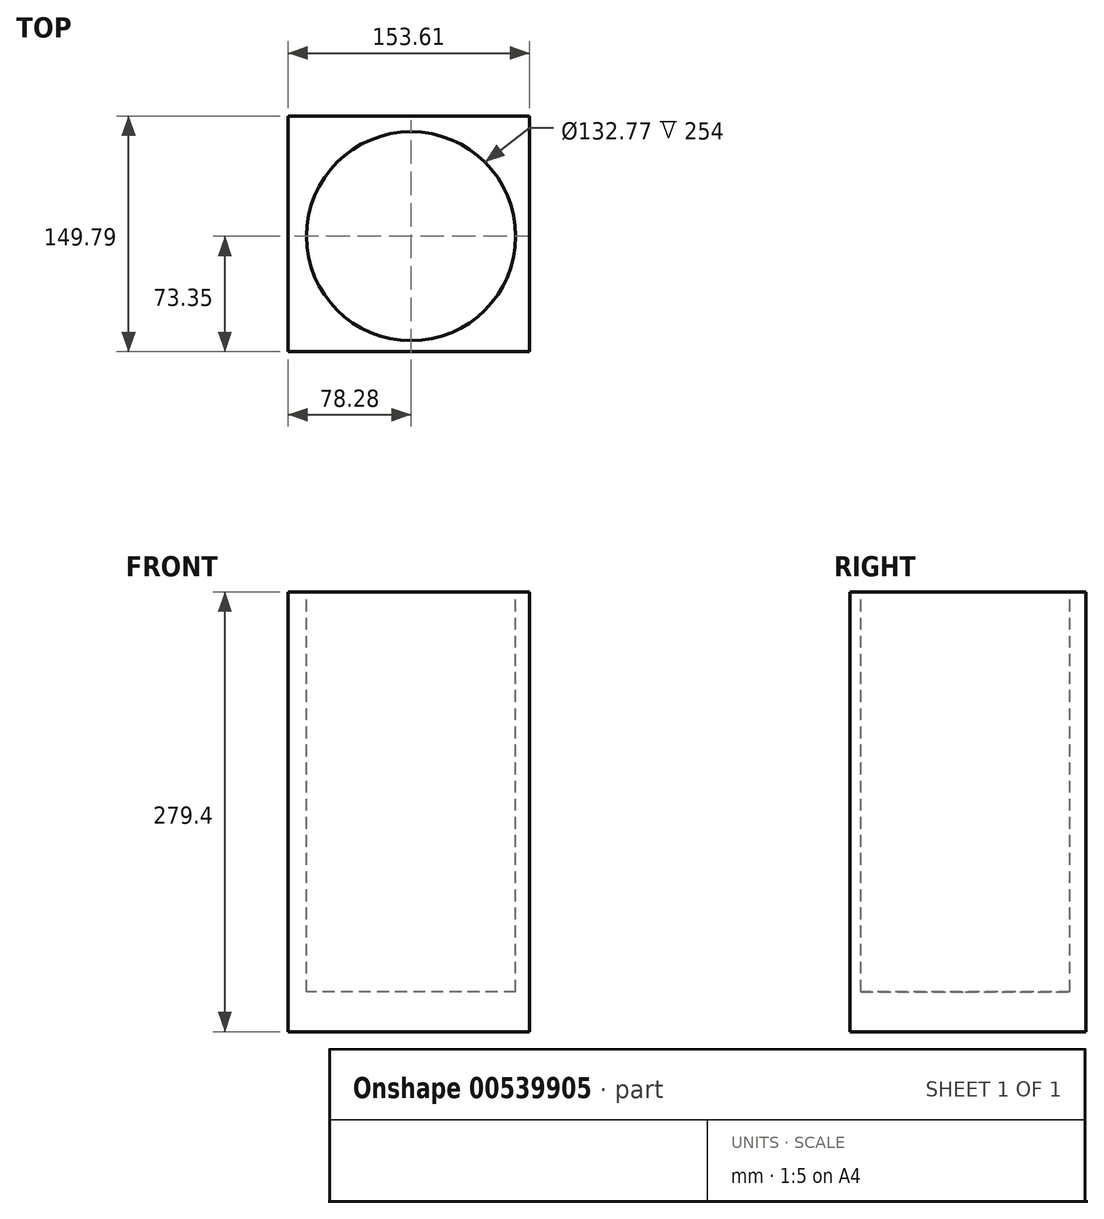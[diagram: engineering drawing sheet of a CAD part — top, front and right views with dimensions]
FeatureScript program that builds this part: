
annotation { "Feature Type Name" : "Feature", "Feature Type Description" : "" }
export const myFeature = defineFeature(function(context is Context, id is Id, definition is map)
    precondition{}
    {
        {
            var Q0;
            Q0=qCreatedBy(makeId("Top.planeOp"),FACE);
            var sketch = newSketch(context, id + "F0", { "sketchPlane" : qUnion([Q0])});
            skLineSegment(sketch, "E0.bottom", {"start": v(75.33, -73.35) * mm, "end": v(-78.28, -73.35) * mm});
            skLineSegment(sketch, "E0.top", {"start": v(75.33, 76.44) * mm, "end": v(-78.28, 76.44) * mm});
            skLineSegment(sketch, "E0.left", {"start": v(75.33, -73.35) * mm, "end": v(75.33, 76.44) * mm});
            skLineSegment(sketch, "E0.right", {"start": v(-78.28, -73.35) * mm, "end": v(-78.28, 76.44) * mm});
            skSolve(sketch);
        }
        {
            var Q0;
            Q0=makeQuery(id+"F0.imprint","IMPRINT",FACE,{"disambiguationData":[TD([[makeQuery(id+"F0.imprint","IMPRINT",EDGE,{"derivedFrom":sQuery(id+"F0.wireOp",EDGE,"E0.bottom")}),-1.0]])]});
            extrude(context, id + "F1", {"entities" : qUnion([Q0]), "depth" : 279.4 * mm, "offsetDistance" : 25.4 * mm});
        }
        {
            var Q0;
            Q0=makeQuery(id+"F1.opExtrude","CAP_FACE",FACE,{"disambiguationData":[OSD([sQuery(id+"F0.wireOp",EDGE,"E0.bottom"),sQuery(id+"F0.wireOp",EDGE,"E0.top"),sQuery(id+"F0.wireOp",EDGE,"E0.left"),sQuery(id+"F0.wireOp",EDGE,"E0.right")])],"isStart":false});
            var sketch = newSketch(context, id + "F2", { "sketchPlane" : qUnion([Q0])});
            skCircle(sketch, "E1", {"center": v(0, 0) * mm, "radius": 66.39 * mm});
            skSolve(sketch);
        }
        {
            var Q0;
            Q0=makeQuery(id+"F2.imprint","IMPRINT",FACE,{"disambiguationData":[TD([[makeQuery(id+"F2.imprint","IMPRINT",EDGE,{"derivedFrom":sQuery(id+"F2.wireOp",EDGE,"E1")}),1.0]])]});
            extrude(context, id + "F3", {"entities" : qUnion([Q0]), "operationType" : NewBodyOperationType.REMOVE, "oppositeDirection" : true, "depth" : 254 * mm, "offsetDistance" : 25.4 * mm});
        }
    });
